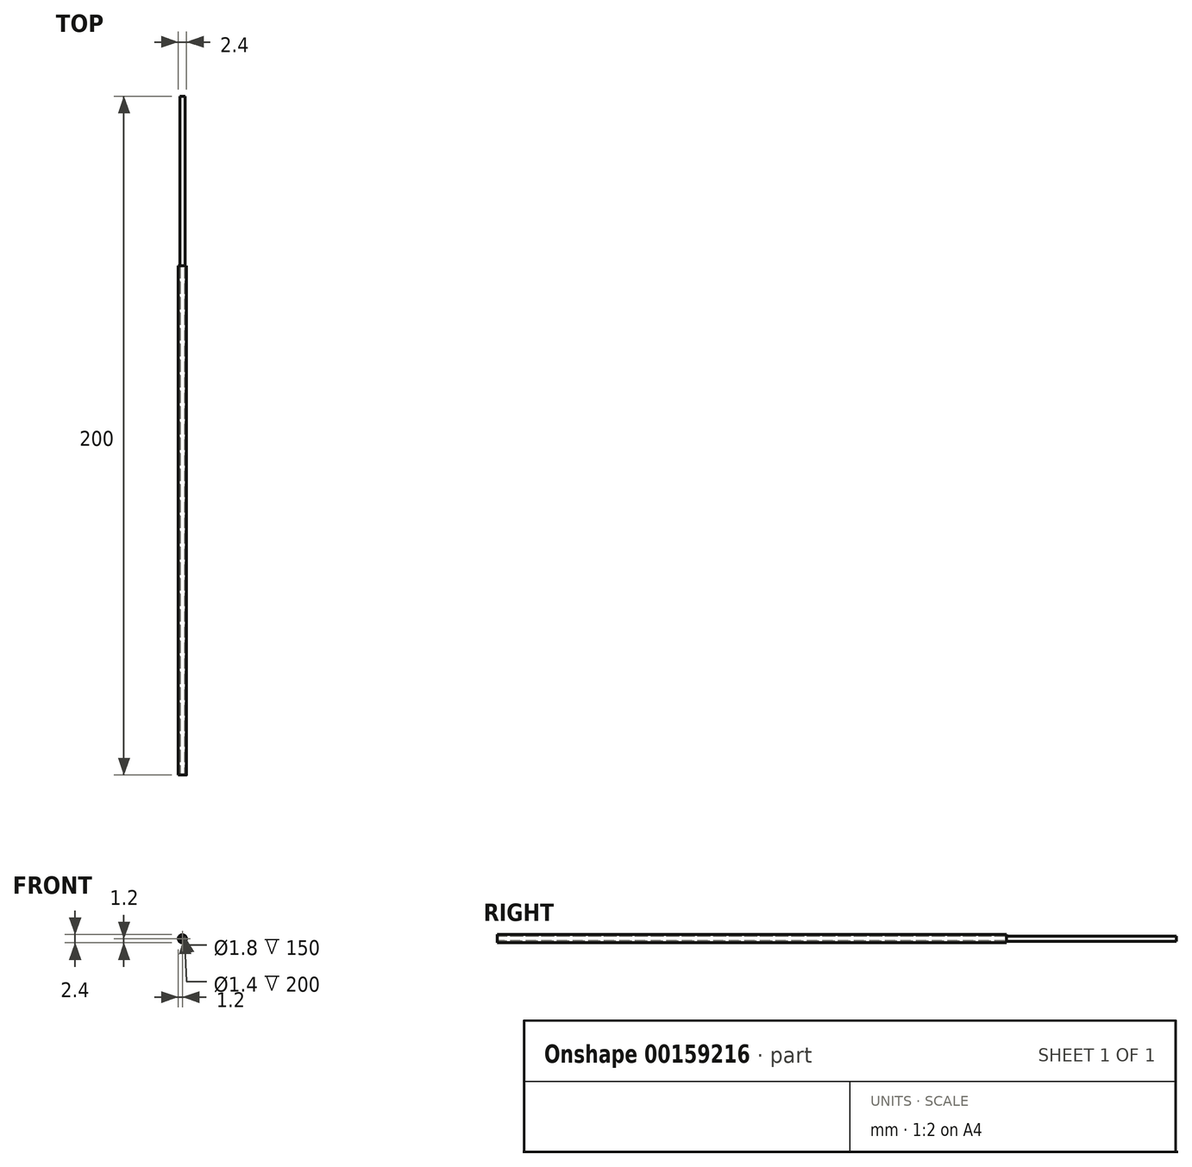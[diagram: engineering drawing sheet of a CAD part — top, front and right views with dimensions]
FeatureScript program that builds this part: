
annotation { "Feature Type Name" : "Feature", "Feature Type Description" : "" }
export const myFeature = defineFeature(function(context is Context, id is Id, definition is map)
    precondition{}
    {
        {
            assignVariable(context, id + "F0", {"name" : "TubeTransmissionLength", "anyValue" : 200});
        }
        {
            assignVariable(context, id + "F1", {"name" : "Angle", "anyValue" : 0});
        }
        {
            var Q0;
            Q0=qCreatedBy(makeId("Front.planeOp"),FACE);
            var sketch = newSketch(context, id + "F2", { "sketchPlane" : qUnion([Q0])});
            skCircle(sketch, "E0", {"center": v(0, 0) * mm, "radius": 0.7 * mm});
            skCircle(sketch, "E1", {"center": v(0, 0) * mm, "radius": 0.8 * mm});
            skSolve(sketch);
        }
        {
            var Q0;
            Q0=qCreatedBy(makeId("Top.planeOp"),FACE);
            var sketch = newSketch(context, id + "F3", { "sketchPlane" : qUnion([Q0])});
            skLineSegment(sketch, "E2", {"start": v(0, 0) * mm, "end": v(0, -200) * mm});
            skLineSegment(sketch, "E3", {"start": v(0, -145.32) * mm, "end": v(0, -200) * mm, "construction": true});
            skLineSegment(sketch, "E4", {"start": v(0, -200) * mm, "end": v(-35, -200) * mm, "construction": true});
            skLineSegment(sketch, "E5", {"start": v(0, -200) * mm, "end": v(0, -200) * mm});
            skSolve(sketch);
        }
        {
            var Q0;
            Q0=makeQuery(id+"F2.imprint","IMPRINT",FACE,{"disambiguationData":[TD([[makeQuery(id+"F2.imprint","IMPRINT",EDGE,{"derivedFrom":sQuery(id+"F2.wireOp",EDGE,"E0")}),-1.0]])]});
            var Q1;
            Q1=sQuery(id+"F3.wireOp",EDGE,"E2");
            var Q2;
            Q2=sQuery(id+"F3.wireOp",EDGE,"E5");
            sweep(context, id + "F4", {"profiles" : qUnion([Q0]), "path" : qUnion([Q1, Q2])});
        }
        {
            var Q0;
            Q0=makeQuery(id+"F4.opSweep","CAP_FACE",FACE,{"disambiguationData":[OSD([sQuery(id+"F2.wireOp",EDGE,"E0"),sQuery(id+"F2.wireOp",EDGE,"E1"),sQuery(id+"F3.wireOp",VERTEX,"E2.start")])],"isStart":true});
            cPlane(context, id + "F5", {"entities" : qUnion([Q0]), "cplaneType" : CPlaneType.OFFSET, "offset" : 50 * mm, "oppositeDirection" : true, "width" : 150 * mm, "height" : 150 * mm});
        }
        {
            var Q0;
            Q0=qCreatedBy(id+"F5.planeOp",FACE);
            var sketch = newSketch(context, id + "F6", { "sketchPlane" : qUnion([Q0])});
            skCircle(sketch, "E6.0", {"center": v(0, 0) * mm, "radius": 0.8 * mm});
            skCircle(sketch, "E6.1", {"center": v(0, 0) * mm, "radius": 0.7 * mm});
            skCircle(sketch, "E7", {"center": v(0, 0) * mm, "radius": 0.9 * mm});
            skCircle(sketch, "E8", {"center": v(0, 0) * mm, "radius": 1.2 * mm});
            skSolve(sketch);
        }
        {
            var Q0;
            Q0=makeQuery(id+"F6.imprint","IMPRINT",FACE,{"disambiguationData":[TD([[makeQuery(id+"F6.imprint","IMPRINT",EDGE,{"derivedFrom":sQuery(id+"F6.wireOp",EDGE,"E7")}),-1.0]])]});
            var Q1;
            Q1=makeQuery(id+"F4.opSweep","SWEPT_FACE",FACE,{"disambiguationData":[OSD([sQuery(id+"F2.wireOp",EDGE,"E1"),sQuery(id+"F3.wireOp",EDGE,"E2")])]});
            extrude(context, id + "F7", {"entities" : qUnion([Q0]), "oppositeDirection" : true, "endBoundEntityFace" : qUnion([Q1]), "depth" : (getVariable(context, 'TubeTransmissionLength') - 50) * mm});
        }
        {
            var Q0;
            Q0=makeQuery(id+"F7.opExtrude","CAP_FACE",FACE,{"disambiguationData":[OSD([sQuery(id+"F6.wireOp",EDGE,"E7"),sQuery(id+"F6.wireOp",EDGE,"E8")])],"isStart":true});
            cPlane(context, id + "F8", {"entities" : qUnion([Q0]), "cplaneType" : CPlaneType.OFFSET, "offset" : 50 * mm, "oppositeDirection" : true, "width" : 150 * mm, "height" : 150 * mm});
        }
        {
            var Q0;
            Q0=qCreatedBy(id+"F8.planeOp",FACE);
            var sketch = newSketch(context, id + "F9", { "sketchPlane" : qUnion([Q0])});
            skCircle(sketch, "E9.0", {"center": v(0, 0) * mm, "radius": 1.2 * mm});
            skLineSegment(sketch, "E10", {"start": v(0, 0) * mm, "end": v(0, 9.07) * mm});
            skLineSegment(sketch, "E11", {"start": v(0, 0) * mm, "end": v(-8.67, 0) * mm});
            skSolve(sketch);
        }
        {
            var Q0;
            Q0=makeQuery(id+"F7.opExtrude","SWEPT_BODY",BODY,{"disambiguationData":[OSD([sQuery(id+"F6.wireOp",EDGE,"E7"),sQuery(id+"F6.wireOp",EDGE,"E8")])]});
            var Q1;
            Q1=makeQuery(id+"F4.opSweep","SWEPT_BODY",BODY,{"disambiguationData":[OSD([sQuery(id+"F2.wireOp",EDGE,"E0"),sQuery(id+"F2.wireOp",EDGE,"E1"),sQuery(id+"F3.wireOp",EDGE,"E5")])]});
            var Q2;
            Q2=sQuery(id+"F9.wireOp",EDGE,"E10");
            transform(context, id + "F10", {"entities" : qUnion([Q0, Q1]), "transformType" : TransformType.ROTATION, "transformAxis" : qUnion([Q2]), "angle" : (getVariable(context, 'Angle')) * degree, "makeCopy" : false});
        }
    });
